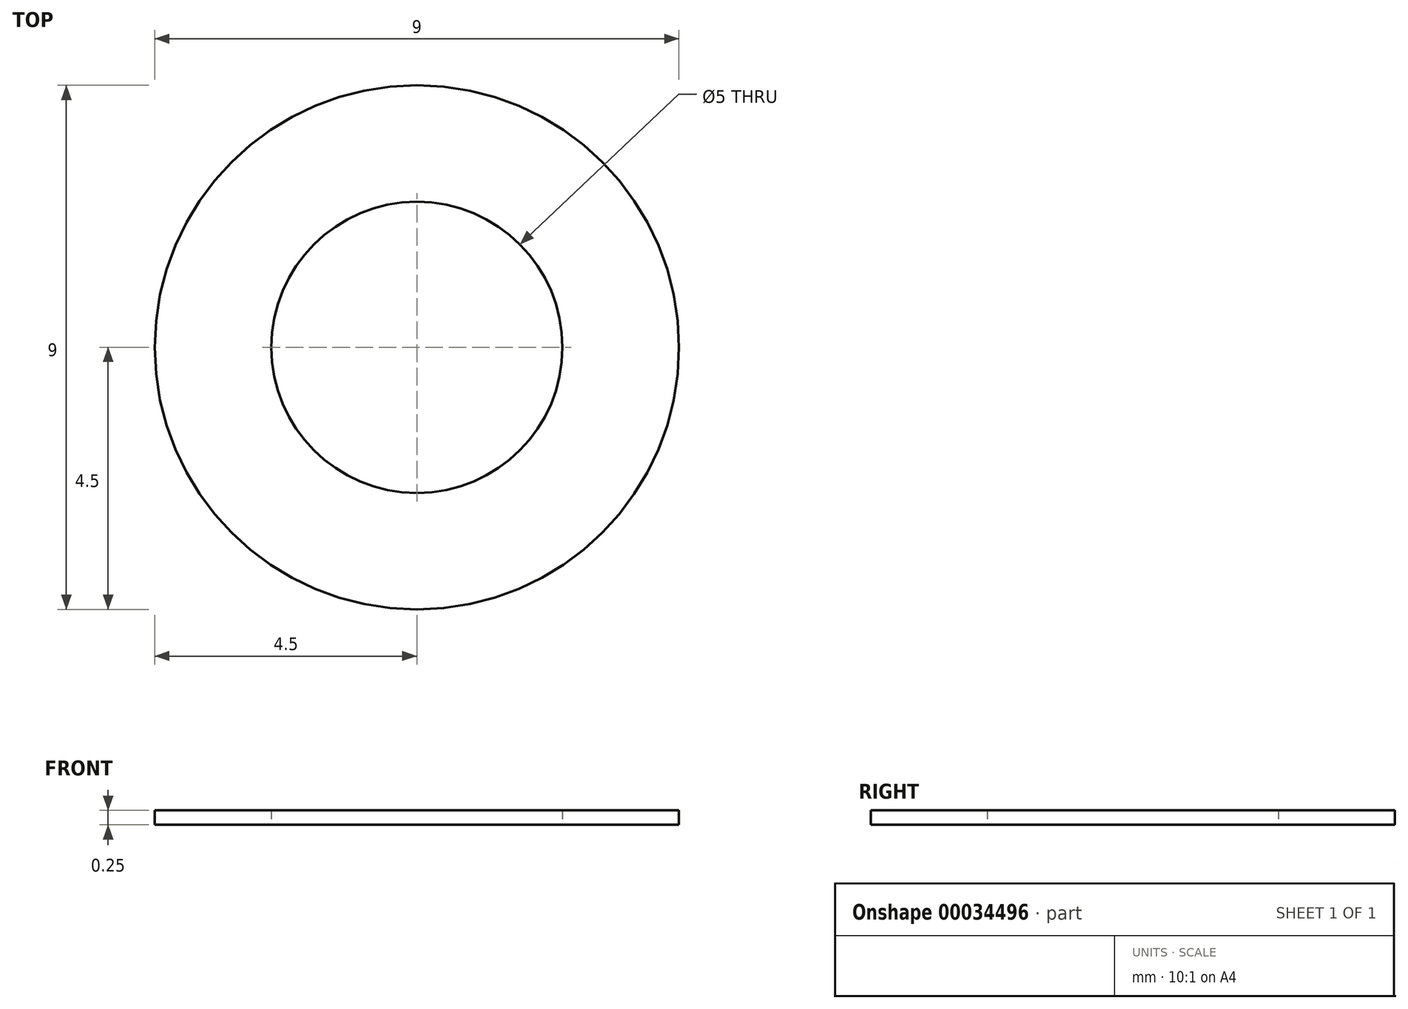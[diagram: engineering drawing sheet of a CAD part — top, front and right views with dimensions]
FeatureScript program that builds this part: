
annotation { "Feature Type Name" : "Feature", "Feature Type Description" : "" }
export const myFeature = defineFeature(function(context is Context, id is Id, definition is map)
    precondition{}
    {
        {
            var Q0;
            Q0=qCreatedBy(makeId("Top.planeOp"),FACE);
            var sketch = newSketch(context, id + "F0", { "sketchPlane" : qUnion([Q0])});
            skCircle(sketch, "E0", {"center": v(0, 0) * mm, "radius": 4.5 * mm});
            skCircle(sketch, "E1", {"center": v(0, 0) * mm, "radius": 2.5 * mm});
            skSolve(sketch);
        }
        {
            var Q0;
            Q0 = qSketchRegion(id + "F0", true);
            extrude(context, id + "F1", {"entities" : qUnion([Q0]), "depth" : 0.25 * mm});
        }
    });
